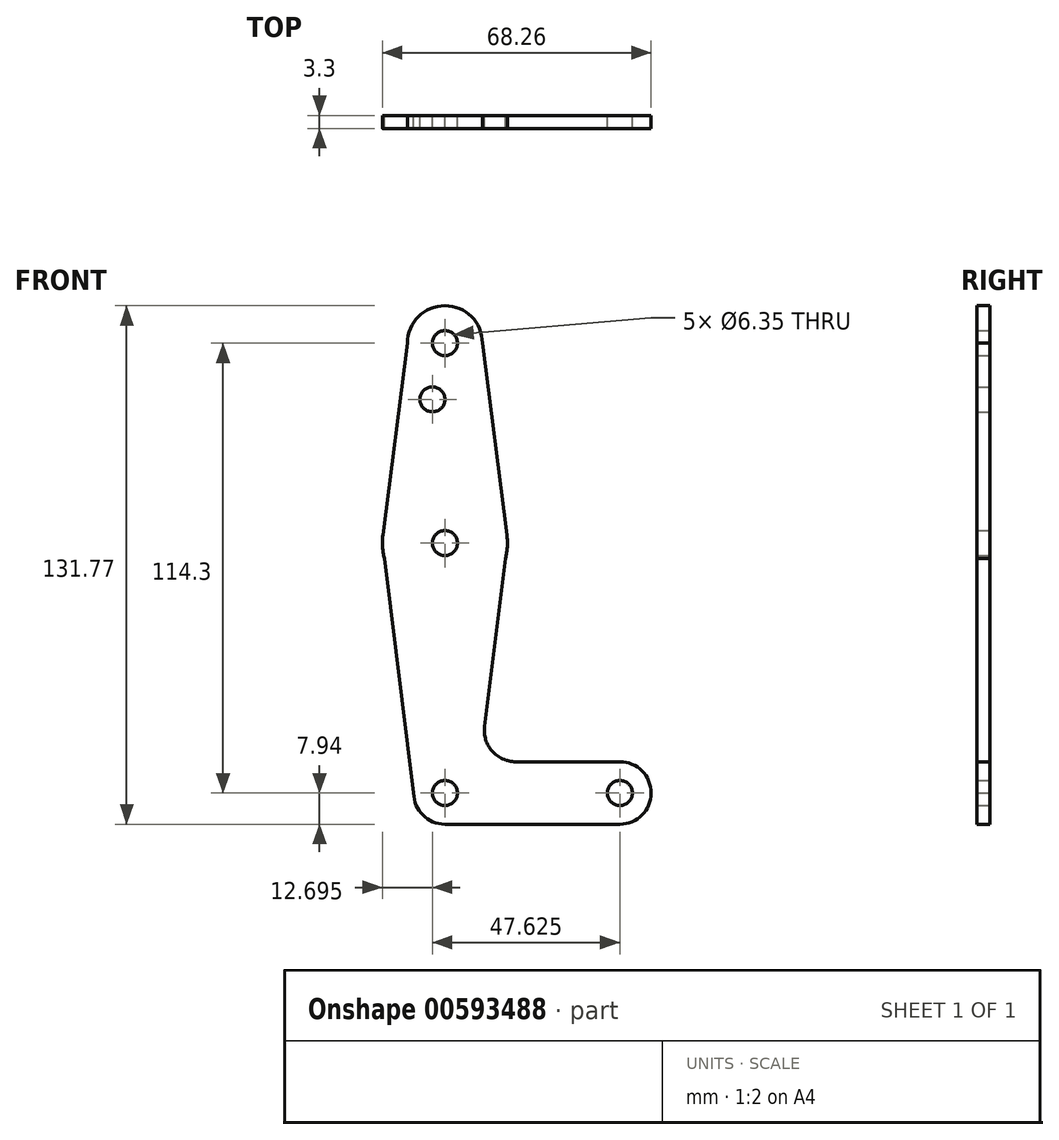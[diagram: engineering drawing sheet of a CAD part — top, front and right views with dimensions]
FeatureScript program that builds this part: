
annotation { "Feature Type Name" : "Feature", "Feature Type Description" : "" }
export const myFeature = defineFeature(function(context is Context, id is Id, definition is map)
    precondition{}
    {
        {
            var Q0;
            Q0=qCreatedBy(makeId("Front.planeOp"),FACE);
            var sketch = newSketch(context, id + "F0", { "sketchPlane" : qUnion([Q0])});
            skCircle(sketch, "E0", {"center": v(0, 114.3) * mm, "radius": 9.53 * mm});
            skCircle(sketch, "E1", {"center": v(0, 63.5) * mm, "radius": 15.88 * mm});
            skCircle(sketch, "E2", {"center": v(0, 0) * mm, "radius": 7.94 * mm});
            skCircle(sketch, "E3", {"center": v(44.45, 0) * mm, "radius": 7.94 * mm});
            skCircle(sketch, "E4", {"center": v(0, 114.3) * mm, "radius": 3.18 * mm});
            skCircle(sketch, "E5", {"center": v(0, 63.5) * mm, "radius": 3.18 * mm});
            skCircle(sketch, "E6", {"center": v(0, 0) * mm, "radius": 3.18 * mm});
            skCircle(sketch, "E7", {"center": v(44.45, 0) * mm, "radius": 3.18 * mm});
            skLineSegment(sketch, "E8", {"start": v(0, -7.94) * mm, "end": v(44.45, -7.94) * mm});
            skCircle(sketch, "E9", {"center": v(-3.17, 100.03) * mm, "radius": 3.18 * mm});
            skPoint(sketch, "E10.newPointA", {"position": v(0, 7.94) * mm});
            skPoint(sketch, "E10.newPointB", {"position": v(7.94, 0) * mm});
            skLineSegment(sketch, "E11", {"start": v(0, 114.3) * mm, "end": v(0, 0) * mm, "construction": true});
            skLineSegment(sketch, "E12", {"start": v(0, 0) * mm, "end": v(44.45, 0) * mm, "construction": true});
            skLineSegment(sketch, "E13", {"start": v(9.52, 114.3) * mm, "end": v(15.75, 65.5) * mm});
            skLineSegment(sketch, "E14", {"start": v(-9.53, 114.3) * mm, "end": v(-15.75, 65.5) * mm});
            skLineSegment(sketch, "E15", {"start": v(-7.94, 0) * mm, "end": v(-15.88, 63.5) * mm});
            skArc(sketch, "E16.filletArc", {"start": v(10.08, 16.89) * mm, "mid": v(12, 10.63) * mm, "end": v(17.97, 7.94) * mm});
            skLineSegment(sketch, "E17", {"start": v(17.97, 7.94) * mm, "end": v(44.45, 7.94) * mm});
            skLineSegment(sketch, "E18", {"start": v(10.08, 16.89) * mm, "end": v(15.87, 63.5) * mm});
            skSolve(sketch);
        }
        {
            var Q0;
            Q0 = qSketchRegion(id + "F0", true);
            extrude(context, id + "F1", {"entities" : qUnion([Q0]), "depth" : 3.3 * mm, "offsetDistance" : 25.4 * mm});
        }
    });
